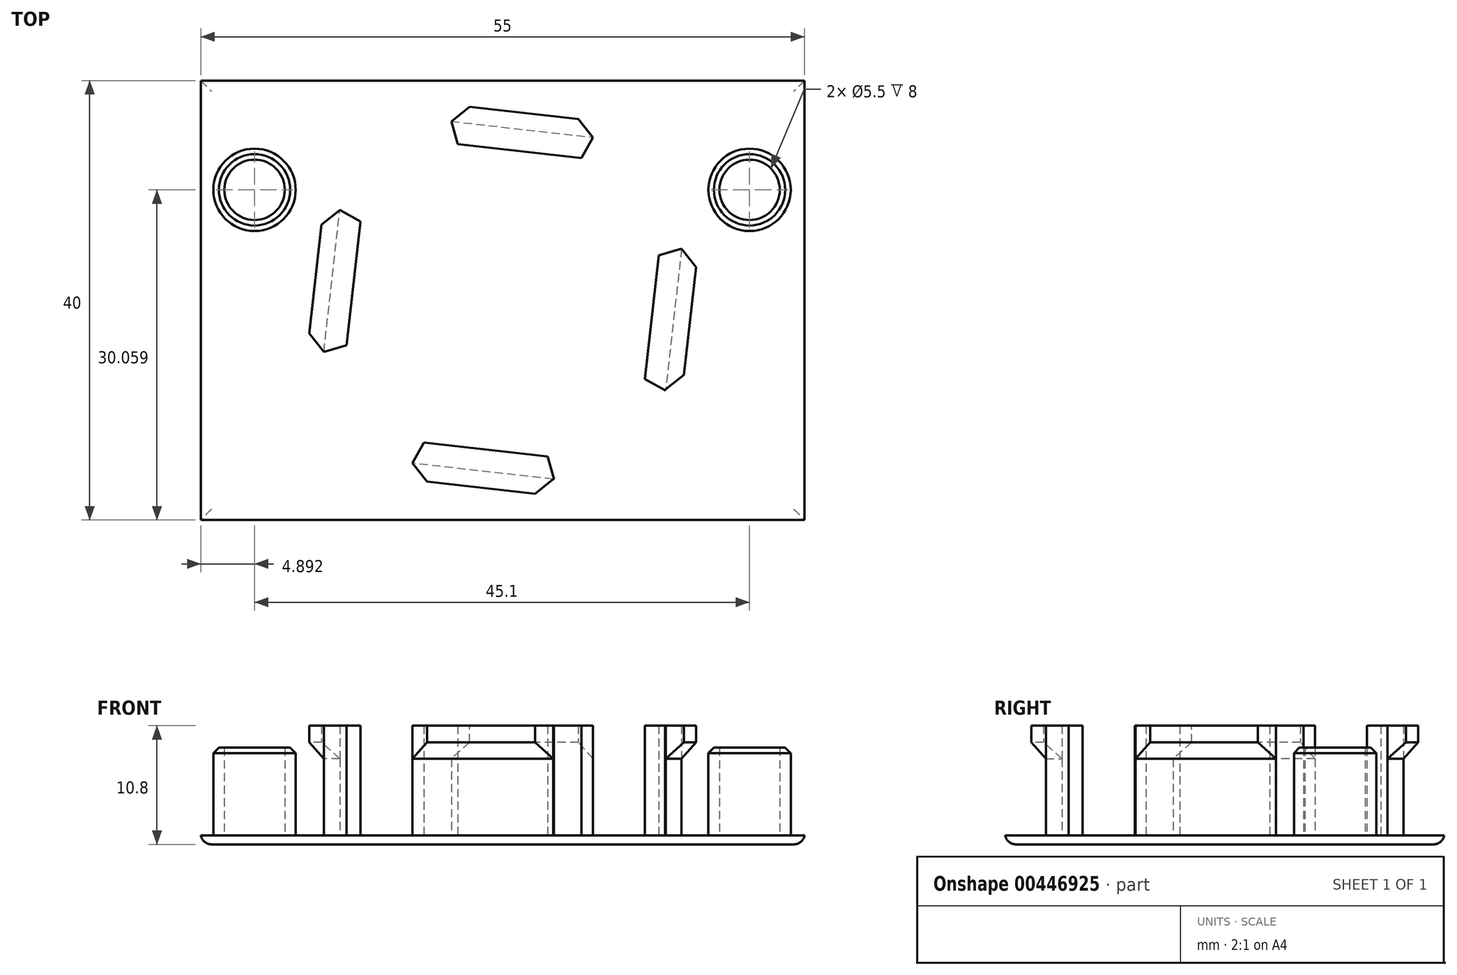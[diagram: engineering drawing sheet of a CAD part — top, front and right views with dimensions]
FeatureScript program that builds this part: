
annotation { "Feature Type Name" : "Feature", "Feature Type Description" : "" }
export const myFeature = defineFeature(function(context is Context, id is Id, definition is map)
    precondition{}
    {
        {
            var Q0;
            Q0=qCreatedBy(makeId("Top.planeOp"),FACE);
            var sketch = newSketch(context, id + "F0", { "sketchPlane" : qUnion([Q0])});
            skLineSegment(sketch, "E0.bottom", {"start": v(27.5, -20) * mm, "end": v(-27.5, -20) * mm});
            skLineSegment(sketch, "E0.top", {"start": v(27.5, 20) * mm, "end": v(-27.5, 20) * mm});
            skLineSegment(sketch, "E0.left", {"start": v(27.5, -20) * mm, "end": v(27.5, 20) * mm});
            skLineSegment(sketch, "E0.right", {"start": v(-27.5, -20) * mm, "end": v(-27.5, 20) * mm});
            skPoint(sketch, "E0.middle", {"position": v(0, 0) * mm});
            skSolve(sketch);
        }
        {
            var Q0;
            Q0=makeQuery(id+"F0.imprint","IMPRINT",FACE,{"disambiguationData":[TD([[makeQuery(id+"F0.imprint","IMPRINT",EDGE,{"derivedFrom":sQuery(id+"F0.wireOp",EDGE,"E0.bottom")}),-1.0]])]});
            extrude(context, id + "F1", {"entities" : qUnion([Q0]), "depth" : .8 * mm, "offsetDistance" : 25 * mm});
        }
        {
            var Q0;
            Q0=makeQuery(id+"F1.opExtrude","CAP_FACE",FACE,{"disambiguationData":[OSD([sQuery(id+"F0.wireOp",EDGE,"E0.bottom"),sQuery(id+"F0.wireOp",EDGE,"E0.top"),sQuery(id+"F0.wireOp",EDGE,"E0.left"),sQuery(id+"F0.wireOp",EDGE,"E0.right")])],"isStart":false});
            var sketch = newSketch(context, id + "F2", { "sketchPlane" : qUnion([Q0])});
            skCircle(sketch, "E1", {"center": v(-22.6, 10.06) * mm, "radius": 4 * mm});
            skCircle(sketch, "E2", {"center": v(22.5, 10.06) * mm, "radius": 4 * mm});
            skCircle(sketch, "E3", {"center": v(-0.06, 0.06) * mm, "radius": 17 * mm});
            skLineSegment(sketch, "E4", {"start": v(-18.6, 10.06) * mm, "end": v(18.5, 10.06) * mm, "construction": true});
            skLineSegment(sketch, "E5", {"start": v(-22.6, 10.06) * mm, "end": v(-18.6, 10.06) * mm, "construction": true});
            skLineSegment(sketch, "E6", {"start": v(22.5, 10.06) * mm, "end": v(18.5, 10.06) * mm, "construction": true});
            skLineSegment(sketch, "E7", {"start": v(-0.06, 0.06) * mm, "end": v(13.4, -10.33) * mm});
            skLineSegment(sketch, "E8", {"start": v(18.8, 11.61) * mm, "end": v(12.41, 11.61) * mm});
            skLineSegment(sketch, "E9", {"start": v(12.41, 11.61) * mm, "end": v(-12.53, 11.61) * mm, "construction": true});
            skLineSegment(sketch, "E10", {"start": v(-12.53, 11.61) * mm, "end": v(-18.92, 11.61) * mm});
            skLineSegment(sketch, "E11", {"start": v(-0.06, 0.06) * mm, "end": v(-0.06, 17.06) * mm, "construction": true});
            skLineSegment(sketch, "E12", {"start": v(-0.06, 17.06) * mm, "end": v(22.5, 17.06) * mm});
            skLineSegment(sketch, "E13", {"start": v(22.5, 10.06) * mm, "end": v(22.5, 14.06) * mm, "construction": true});
            skLineSegment(sketch, "E14", {"start": v(22.5, 14.06) * mm, "end": v(22.5, 17.06) * mm});
            skCircle(sketch, "E15", {"center": v(22.5, 10.06) * mm, "radius": 3.75 * mm});
            skCircle(sketch, "E16", {"center": v(-22.6, 10.06) * mm, "radius": 3.75 * mm});
            skCircle(sketch, "E17.cCircle", {"center": v(0, 0) * mm, "radius": 15.67 * mm, "construction": true});
            skLineSegment(sketch, "E17.0", {"start": v(16.3, 4.68) * mm, "end": v(14.84, -8.21) * mm});
            skLineSegment(sketch, "E17.1", {"start": v(14.84, -8.21) * mm, "end": v(4.68, -16.3) * mm});
            skLineSegment(sketch, "E17.2", {"start": v(4.68, -16.3) * mm, "end": v(-8.21, -14.84) * mm});
            skLineSegment(sketch, "E17.3", {"start": v(-8.21, -14.84) * mm, "end": v(-16.3, -4.68) * mm});
            skLineSegment(sketch, "E17.4", {"start": v(-16.3, -4.68) * mm, "end": v(-14.84, 8.21) * mm});
            skLineSegment(sketch, "E17.5", {"start": v(-14.84, 8.21) * mm, "end": v(-4.68, 16.3) * mm});
            skLineSegment(sketch, "E17.6", {"start": v(-4.68, 16.3) * mm, "end": v(8.21, 14.84) * mm});
            skLineSegment(sketch, "E17.7", {"start": v(8.21, 14.84) * mm, "end": v(16.3, 4.68) * mm});
            skPoint(sketch, "E17.0.midPoint", {"position": v(15.57, -1.76) * mm});
            skLineSegment(sketch, "E18.0", {"start": v(-12.94, 7.17) * mm, "end": v(-4.09, 14.22) * mm});
            skLineSegment(sketch, "E18.1", {"start": v(-14.22, -4.09) * mm, "end": v(-12.94, 7.17) * mm});
            skLineSegment(sketch, "E18.2", {"start": v(-4.09, 14.22) * mm, "end": v(7.17, 12.94) * mm});
            skLineSegment(sketch, "E18.3", {"start": v(-7.17, -12.94) * mm, "end": v(-14.22, -4.09) * mm});
            skLineSegment(sketch, "E18.4", {"start": v(7.17, 12.94) * mm, "end": v(14.22, 4.09) * mm});
            skLineSegment(sketch, "E18.5", {"start": v(14.22, 4.09) * mm, "end": v(12.94, -7.17) * mm});
            skLineSegment(sketch, "E18.6", {"start": v(12.94, -7.17) * mm, "end": v(4.09, -14.22) * mm});
            skLineSegment(sketch, "E18.7", {"start": v(4.09, -14.22) * mm, "end": v(-7.17, -12.94) * mm});
            skLineSegment(sketch, "E19", {"start": v(8.21, 14.84) * mm, "end": v(7.17, 12.94) * mm});
            skLineSegment(sketch, "E20", {"start": v(16.3, 4.68) * mm, "end": v(14.22, 4.09) * mm});
            skLineSegment(sketch, "E21", {"start": v(14.84, -8.21) * mm, "end": v(12.94, -7.17) * mm});
            skLineSegment(sketch, "E22", {"start": v(4.68, -16.3) * mm, "end": v(4.09, -14.22) * mm});
            skLineSegment(sketch, "E23", {"start": v(-8.21, -14.84) * mm, "end": v(-7.17, -12.94) * mm});
            skLineSegment(sketch, "E24", {"start": v(-16.3, -4.68) * mm, "end": v(-14.22, -4.09) * mm});
            skLineSegment(sketch, "E25", {"start": v(-12.94, 7.17) * mm, "end": v(-14.84, 8.21) * mm});
            skLineSegment(sketch, "E26", {"start": v(-4.09, 14.22) * mm, "end": v(-4.68, 16.3) * mm});
            skCircle(sketch, "E27.0", {"center": v(-22.6, 10.06) * mm, "radius": 2.75 * mm});
            skLineSegment(sketch, "E28.0", {"start": v(32.5, -25) * mm, "end": v(32.5, 25) * mm});
            skLineSegment(sketch, "E28.1", {"start": v(-32.5, -25) * mm, "end": v(32.5, -25) * mm});
            skLineSegment(sketch, "E28.2", {"start": v(-32.5, 25) * mm, "end": v(-32.5, -25) * mm});
            skLineSegment(sketch, "E28.3", {"start": v(32.5, 25) * mm, "end": v(-32.5, 25) * mm});
            skCircle(sketch, "E29.0", {"center": v(22.5, 10.06) * mm, "radius": 2.75 * mm});
            skSolve(sketch);
        }
        {
            var Q0;
            Q0=makeQuery(id+"F2.imprint","IMPRINT",FACE,{"disambiguationData":[TD([[makeQuery(id+"F2.imprint","IMPRINT",EDGE,{"derivedFrom":sQuery(id+"F2.wireOp",EDGE,"E17.6")}),-1.0]])]});
            var Q1;
            {var subQ1=sQuery(id+"F2.wireOp",EDGE,"E18.7");Q1=makeQuery(id+"F2.imprint","IMPRINT",FACE,{"disambiguationData":[TD([[makeQuery(id+"F2.imprint","IMPRINT",EDGE,{"derivedFrom":subQ1}),1.0]])]});}
            var Q2;
            Q2=makeQuery(id+"F2.imprint","IMPRINT",FACE,{"disambiguationData":[TD([[makeQuery(id+"F2.imprint","IMPRINT",EDGE,{"derivedFrom":sQuery(id+"F2.wireOp",EDGE,"E17.4")}),-1.0]])]});
            var Q3;
            {var subQ1=sQuery(id+"F2.wireOp",EDGE,"E18.5");Q3=makeQuery(id+"F2.imprint","IMPRINT",FACE,{"disambiguationData":[TD([[makeQuery(id+"F2.imprint","IMPRINT",EDGE,{"derivedFrom":subQ1}),1.0]])]});}
            extrude(context, id + "F3", {"entities" : qUnion([Q0, Q1, Q2, Q3]), "operationType" : NewBodyOperationType.ADD, "depth" : 10 * mm, "offsetDistance" : 25 * mm});
        }
        {
            var Q0;
            Q0=makeQuery(id+"F2.imprint","IMPRINT",FACE,{"disambiguationData":[TD([[makeQuery(id+"F2.imprint","IMPRINT",EDGE,{"derivedFrom":sQuery(id+"F2.wireOp",EDGE,"E15")}),1.0]])]});
            var Q1;
            Q1=makeQuery(id+"F2.imprint","IMPRINT",FACE,{"disambiguationData":[TD([[makeQuery(id+"F2.imprint","IMPRINT",EDGE,{"derivedFrom":sQuery(id+"F2.wireOp",EDGE,"E16")}),1.0]])]});
            extrude(context, id + "F4", {"entities" : qUnion([Q0, Q1]), "operationType" : NewBodyOperationType.ADD, "depth" : 8 * mm, "offsetDistance" : 25 * mm});
        }
        {
            var Q0;
            Q0=makeQuery(id+"F4.opExtrude","CAP_EDGE",EDGE,{"disambiguationData":[OSD([sQuery(id+"F2.wireOp",EDGE,"E16")])],"isStart":false});
            var Q1;
            Q1=makeQuery(id+"F4.opExtrude","CAP_EDGE",EDGE,{"disambiguationData":[OSD([sQuery(id+"F2.wireOp",EDGE,"E15")])],"isStart":false});
            chamfer(context, id + "F5", {"entities" : qUnion([Q0, Q1]), "width" : .5 * mm, "tangentPropagation" : true});
        }
        {
            var Q0;
            Q0=makeQuery(id+"F3.opExtrude","SWEPT_FACE",FACE,{"disambiguationData":[OSD([sQuery(id+"F2.wireOp",EDGE,"E17.2")])]});
            var sketch = newSketch(context, id + "F6", { "sketchPlane" : qUnion([Q0])});
            skPoint(sketch, "E30.0", {"position": v(6.4, 10.8) * mm});
            skPoint(sketch, "E30.1", {"position": v(-6.5, 10.8) * mm});
            skLineSegment(sketch, "E31.bottom", {"start": v(6.4, 10.8) * mm, "end": v(-6.5, 10.8) * mm});
            skLineSegment(sketch, "E31.top", {"start": v(6.4, 7.8) * mm, "end": v(-6.5, 7.8) * mm});
            skLineSegment(sketch, "E31.left", {"start": v(6.4, 10.8) * mm, "end": v(6.4, 7.8) * mm});
            skLineSegment(sketch, "E31.right", {"start": v(-6.5, 10.8) * mm, "end": v(-6.5, 7.8) * mm});
            skSolve(sketch);
        }
        {
            var Q0;
            Q0=makeQuery(id+"F6.imprint","IMPRINT",FACE,{"disambiguationData":[TD([[makeQuery(id+"F6.imprint","IMPRINT",EDGE,{"derivedFrom":sQuery(id+"F6.wireOp",EDGE,"E31.bottom")}),1.0]])]});
            extrude(context, id + "F7", {"entities" : qUnion([Q0]), "operationType" : NewBodyOperationType.ADD, "depth" : 1.5 * mm, "offsetDistance" : 25 * mm});
        }
        {
            var Q0;
            Q0=makeQuery(id+"F7.opExtrude","CAP_EDGE",EDGE,{"disambiguationData":[OSD([sQuery(id+"F6.wireOp",EDGE,"E31.top")])],"isStart":false});
            chamfer(context, id + "F8", {"entities" : qUnion([Q0]), "width" : 1.5 * mm, "tangentPropagation" : true});
        }
        {
            var Q0;
            Q0=makeQuery(id+"F7.opExtrude","CAP_EDGE",EDGE,{"disambiguationData":[OSD([sQuery(id+"F6.wireOp",EDGE,"E31.right")])],"isStart":false});
            var Q1;
            Q1=makeQuery(id+"F7.opExtrude","CAP_EDGE",EDGE,{"disambiguationData":[OSD([sQuery(id+"F6.wireOp",EDGE,"E31.left")])],"isStart":false});
            chamfer(context, id + "F9", {"entities" : qUnion([Q0, Q1]), "width" : 1.5 * mm});
        }
        {
            var Q0;
            Q0=makeQuery(id+"F3.opExtrude","SWEPT_FACE",FACE,{"disambiguationData":[OSD([sQuery(id+"F2.wireOp",EDGE,"E17.0")])]});
            var sketch = newSketch(context, id + "F10", { "sketchPlane" : qUnion([Q0])});
            skPoint(sketch, "E32.0", {"position": v(6.5, 10.8) * mm});
            skPoint(sketch, "E32.1", {"position": v(-6.39, 10.8) * mm});
            skLineSegment(sketch, "E33.bottom", {"start": v(-6.39, 10.8) * mm, "end": v(6.5, 10.8) * mm});
            skLineSegment(sketch, "E33.top", {"start": v(-6.39, 7.8) * mm, "end": v(6.5, 7.8) * mm});
            skLineSegment(sketch, "E33.left", {"start": v(-6.39, 10.8) * mm, "end": v(-6.39, 7.8) * mm});
            skLineSegment(sketch, "E33.right", {"start": v(6.5, 10.8) * mm, "end": v(6.5, 7.8) * mm});
            skSolve(sketch);
        }
        {
            var Q0;
            Q0=makeQuery(id+"F10.imprint","IMPRINT",FACE,{"disambiguationData":[TD([[makeQuery(id+"F10.imprint","IMPRINT",EDGE,{"derivedFrom":sQuery(id+"F10.wireOp",EDGE,"E33.bottom")}),1.0]])]});
            extrude(context, id + "F11", {"entities" : qUnion([Q0]), "operationType" : NewBodyOperationType.ADD, "depth" : 1.5 * mm, "offsetDistance" : 25 * mm});
        }
        {
            var Q0;
            Q0=makeQuery(id+"F11.opExtrude","CAP_EDGE",EDGE,{"disambiguationData":[OSD([sQuery(id+"F10.wireOp",EDGE,"E33.top")])],"isStart":false});
            var Q1;
            Q1=makeQuery(id+"F11.opExtrude","CAP_EDGE",EDGE,{"disambiguationData":[OSD([sQuery(id+"F10.wireOp",EDGE,"E33.left")])],"isStart":false});
            var Q2;
            Q2=makeQuery(id+"F11.opExtrude","CAP_EDGE",EDGE,{"disambiguationData":[OSD([sQuery(id+"F10.wireOp",EDGE,"E33.right")])],"isStart":false});
            chamfer(context, id + "F12", {"entities" : qUnion([Q0, Q1, Q2]), "width" : 1.5 * mm, "tangentPropagation" : true});
        }
        {
            var Q0;
            Q0=makeQuery(id+"F3.opExtrude","SWEPT_FACE",FACE,{"disambiguationData":[OSD([sQuery(id+"F2.wireOp",EDGE,"E17.6")])]});
            var sketch = newSketch(context, id + "F13", { "sketchPlane" : qUnion([Q0])});
            skPoint(sketch, "E34.0", {"position": v(-6.5, 10.8) * mm});
            skPoint(sketch, "E34.1", {"position": v(6.5, 10.8) * mm});
            skLineSegment(sketch, "E35.bottom", {"start": v(-6.5, 10.8) * mm, "end": v(6.5, 10.8) * mm});
            skLineSegment(sketch, "E35.top", {"start": v(-6.5, 7.8) * mm, "end": v(6.5, 7.8) * mm});
            skLineSegment(sketch, "E35.left", {"start": v(-6.5, 10.8) * mm, "end": v(-6.5, 7.8) * mm});
            skLineSegment(sketch, "E35.right", {"start": v(6.5, 10.8) * mm, "end": v(6.5, 7.8) * mm});
            skSolve(sketch);
        }
        {
            var Q0;
            Q0=makeQuery(id+"F13.imprint","IMPRINT",FACE,{"disambiguationData":[TD([[makeQuery(id+"F13.imprint","IMPRINT",EDGE,{"derivedFrom":sQuery(id+"F13.wireOp",EDGE,"E35.bottom")}),1.0]])]});
            extrude(context, id + "F14", {"entities" : qUnion([Q0]), "operationType" : NewBodyOperationType.ADD, "depth" : 1.5 * mm, "offsetDistance" : 25 * mm});
        }
        {
            var Q0;
            Q0=makeQuery(id+"F14.opExtrude","CAP_EDGE",EDGE,{"disambiguationData":[OSD([sQuery(id+"F13.wireOp",EDGE,"E35.left")])],"isStart":false});
            var Q1;
            Q1=makeQuery(id+"F14.opExtrude","CAP_EDGE",EDGE,{"disambiguationData":[OSD([sQuery(id+"F13.wireOp",EDGE,"E35.top")])],"isStart":false});
            var Q2;
            Q2=makeQuery(id+"F14.opExtrude","CAP_EDGE",EDGE,{"disambiguationData":[OSD([sQuery(id+"F13.wireOp",EDGE,"E35.right")])],"isStart":false});
            chamfer(context, id + "F15", {"entities" : qUnion([Q0, Q1, Q2]), "width" : 1.5 * mm, "tangentPropagation" : true});
        }
        {
            var Q0;
            Q0=makeQuery(id+"F3.opExtrude","SWEPT_FACE",FACE,{"disambiguationData":[OSD([sQuery(id+"F2.wireOp",EDGE,"E17.4")])]});
            var sketch = newSketch(context, id + "F16", { "sketchPlane" : qUnion([Q0])});
            skPoint(sketch, "E36.0", {"position": v(-6.5, 10.8) * mm});
            skPoint(sketch, "E36.1", {"position": v(6.5, 10.8) * mm});
            skLineSegment(sketch, "E37.bottom", {"start": v(-6.5, 10.8) * mm, "end": v(6.5, 10.8) * mm});
            skLineSegment(sketch, "E37.top", {"start": v(-6.5, 7.8) * mm, "end": v(6.5, 7.8) * mm});
            skLineSegment(sketch, "E37.left", {"start": v(-6.5, 10.8) * mm, "end": v(-6.5, 7.8) * mm});
            skLineSegment(sketch, "E37.right", {"start": v(6.5, 10.8) * mm, "end": v(6.5, 7.8) * mm});
            skSolve(sketch);
        }
        {
            var Q0;
            Q0=makeQuery(id+"F16.imprint","IMPRINT",FACE,{"disambiguationData":[TD([[makeQuery(id+"F16.imprint","IMPRINT",EDGE,{"derivedFrom":sQuery(id+"F16.wireOp",EDGE,"E37.bottom")}),1.0]])]});
            extrude(context, id + "F17", {"entities" : qUnion([Q0]), "operationType" : NewBodyOperationType.ADD, "depth" : 1.5 * mm, "offsetDistance" : 25 * mm});
        }
        {
            var Q0;
            Q0=makeQuery(id+"F17.opExtrude","CAP_EDGE",EDGE,{"disambiguationData":[OSD([sQuery(id+"F16.wireOp",EDGE,"E37.left")])],"isStart":false});
            var Q1;
            Q1=makeQuery(id+"F17.opExtrude","CAP_EDGE",EDGE,{"disambiguationData":[OSD([sQuery(id+"F16.wireOp",EDGE,"E37.top")])],"isStart":false});
            var Q2;
            Q2=makeQuery(id+"F17.opExtrude","CAP_EDGE",EDGE,{"disambiguationData":[OSD([sQuery(id+"F16.wireOp",EDGE,"E37.right")])],"isStart":false});
            chamfer(context, id + "F18", {"entities" : qUnion([Q0, Q1, Q2]), "width" : 1.5 * mm, "tangentPropagation" : true});
        }
        {
            var Q0;
            Q0=makeQuery(id+"F1.opExtrude","CAP_FACE",FACE,{"disambiguationData":[OSD([sQuery(id+"F0.wireOp",EDGE,"E0.bottom"),sQuery(id+"F0.wireOp",EDGE,"E0.top"),sQuery(id+"F0.wireOp",EDGE,"E0.left"),sQuery(id+"F0.wireOp",EDGE,"E0.right")])],"isStart":true});
            fillet(context, id + "F19", {"entities" : qUnion([Q0]), "tangentPropagation" : true, "radius" : 1 * mm, "defaultsChanged" : true, "vertexSettings" : [], "allowEdgeOverflow" : false});
        }
    });
